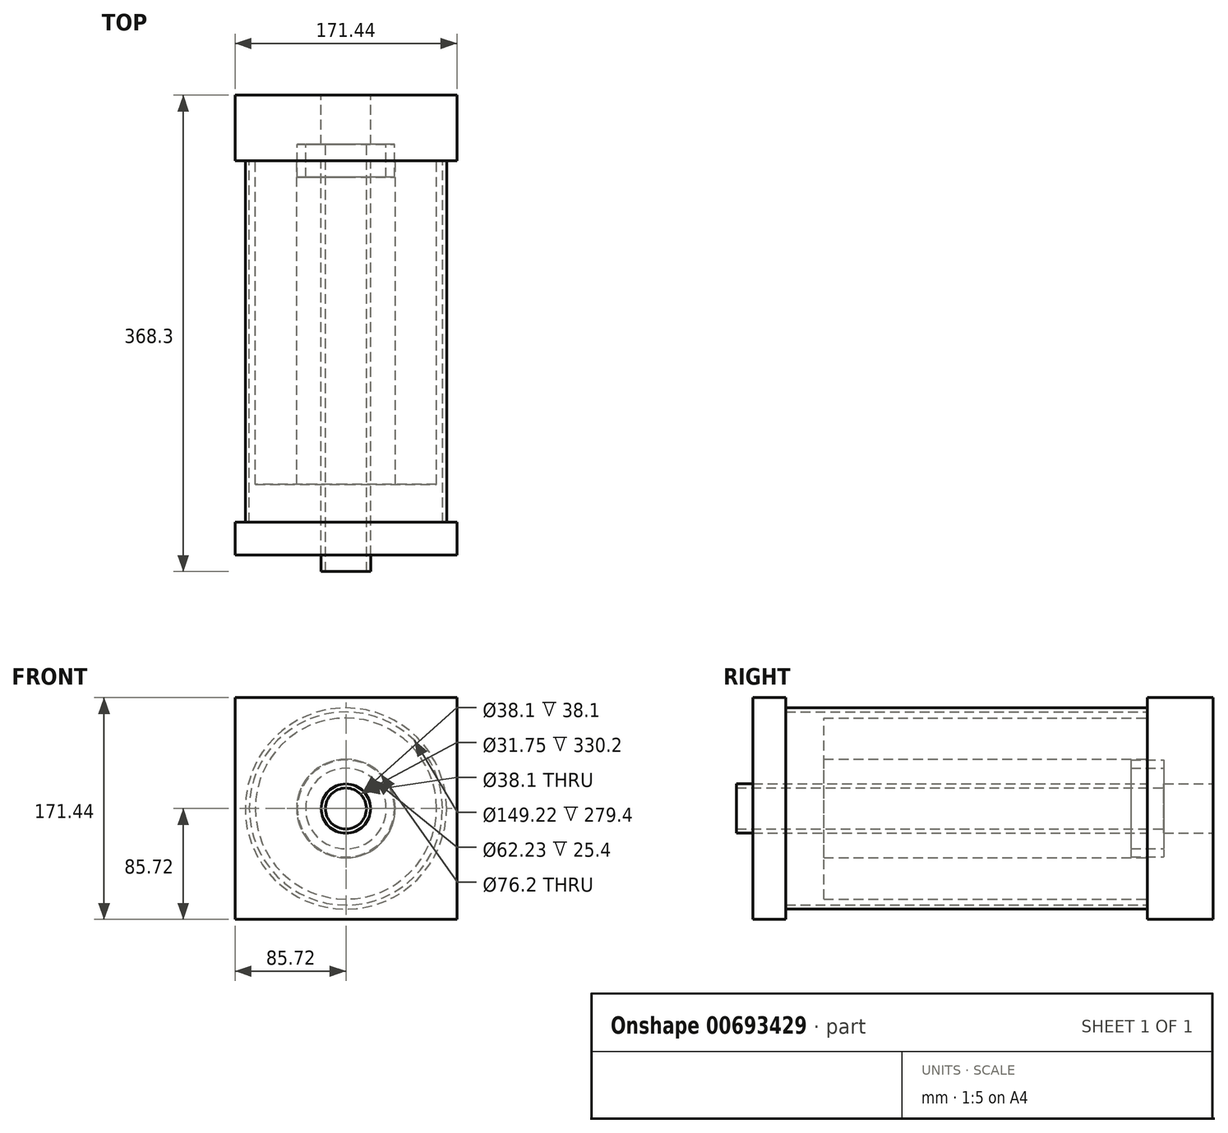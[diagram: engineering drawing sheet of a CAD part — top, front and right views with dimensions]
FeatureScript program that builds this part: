
annotation { "Feature Type Name" : "Feature", "Feature Type Description" : "" }
export const myFeature = defineFeature(function(context is Context, id is Id, definition is map)
    precondition{}
    {
        {
            var Q0;
            Q0=qCreatedBy(makeId("Front.planeOp"),FACE);
            var sketch = newSketch(context, id + "F0", { "sketchPlane" : qUnion([Q0])});
            skCircle(sketch, "E0", {"center": v(0, 0) * mm, "radius": 70 * mm});
            skSolve(sketch);
        }
        {
            var Q0;
            Q0 = qSketchRegion(id + "F0", true);
            extrude(context, id + "F1", {"entities" : qUnion([Q0]), "depth" : 250 * mm, "offsetDistance" : 25.4 * mm});
        }
        {
            var Q0;
            Q0=makeQuery(id+"F1.opExtrude","CAP_FACE",FACE,{"disambiguationData":[OSD([sQuery(id+"F0.wireOp",EDGE,"E0")])],"isStart":true});
            var sketch = newSketch(context, id + "F2", { "sketchPlane" : qUnion([Q0])});
            skCircle(sketch, "E1", {"center": v(0, 0) * mm, "radius": 38.1 * mm});
            skSolve(sketch);
        }
        {
            var Q0;
            Q0 = qSketchRegion(id + "F2", true);
            extrude(context, id + "F3", {"entities" : qUnion([Q0]), "operationType" : NewBodyOperationType.REMOVE, "endBound" : BoundingType.THROUGH_ALL, "oppositeDirection" : true, "depth" : 25.4 * mm, "offsetDistance" : 25.4 * mm});
        }
        {
            var Q0;
            Q0=makeQuery(id+"F1.opExtrude","CAP_FACE",FACE,{"disambiguationData":[OSD([sQuery(id+"F0.wireOp",EDGE,"E0")])],"isStart":true});
            var sketch = newSketch(context, id + "F4", { "sketchPlane" : qUnion([Q0])});
            skCircle(sketch, "E2", {"center": v(0, 0) * mm, "radius": 37.47 * mm});
            skCircle(sketch, "E3", {"center": v(0, 0) * mm, "radius": 31.12 * mm});
            skSolve(sketch);
        }
        {
            var Q0;
            Q0 = qSketchRegion(id + "F4", true);
            extrude(context, id + "F5", {"entities" : qUnion([Q0]), "endBound" : BoundingType.SYMMETRIC, "oppositeDirection" : true, "depth" : 25.4 * mm, "offsetDistance" : 25.4 * mm});
        }
        {
            var Q0;
            Q0=qCreatedBy(makeId("Front.planeOp"),FACE);
            var sketch = newSketch(context, id + "F6", { "sketchPlane" : qUnion([Q0])});
            skCircle(sketch, "E4", {"center": v(0, 0) * mm, "radius": 74.61 * mm});
            skCircle(sketch, "E5", {"center": v(0, 0) * mm, "radius": 77.79 * mm});
            skSolve(sketch);
        }
        {
            var Q0;
            Q0 = qSketchRegion(id + "F6", true);
            extrude(context, id + "F7", {"entities" : qUnion([Q0]), "depth" : 279.4 * mm, "offsetDistance" : 25.4 * mm});
        }
        {
            var Q0;
            Q0=qCreatedBy(makeId("Front.planeOp"),FACE);
            var sketch = newSketch(context, id + "F8", { "sketchPlane" : qUnion([Q0])});
            skLineSegment(sketch, "E6.bottom", {"start": v(-85.73, 85.73) * mm, "end": v(85.73, 85.73) * mm});
            skLineSegment(sketch, "E6.top", {"start": v(-85.73, -85.73) * mm, "end": v(85.73, -85.73) * mm});
            skLineSegment(sketch, "E6.left", {"start": v(-85.73, 85.73) * mm, "end": v(-85.73, -85.73) * mm});
            skLineSegment(sketch, "E6.right", {"start": v(85.73, 85.73) * mm, "end": v(85.73, -85.73) * mm});
            skPoint(sketch, "E6.middle", {"position": v(0, 0) * mm});
            skSolve(sketch);
        }
        {
            var Q0;
            Q0 = qSketchRegion(id + "F8", true);
            extrude(context, id + "F9", {"entities" : qUnion([Q0]), "oppositeDirection" : true, "depth" : 50.8 * mm, "offsetDistance" : 25.4 * mm});
        }
        {
            var Q0;
            Q0=makeQuery(id+"F9.opExtrude","CAP_FACE",FACE,{"disambiguationData":[OSD([sQuery(id+"F8.wireOp",EDGE,"E6.bottom"),sQuery(id+"F8.wireOp",EDGE,"E6.top"),sQuery(id+"F8.wireOp",EDGE,"E6.left"),sQuery(id+"F8.wireOp",EDGE,"E6.right")])],"isStart":false});
            var sketch = newSketch(context, id + "F10", { "sketchPlane" : qUnion([Q0])});
            skCircle(sketch, "E7", {"center": v(0, 0) * mm, "radius": 19.05 * mm});
            skSolve(sketch);
        }
        {
            var Q0;
            Q0 = qSketchRegion(id + "F10", true);
            extrude(context, id + "F11", {"entities" : qUnion([Q0]), "operationType" : NewBodyOperationType.REMOVE, "endBound" : BoundingType.THROUGH_ALL, "oppositeDirection" : true, "depth" : 25.4 * mm, "offsetDistance" : 25.4 * mm});
        }
        {
            var Q0;
            Q0=makeQuery(id+"F9.opExtrude","CAP_FACE",FACE,{"disambiguationData":[OSD([sQuery(id+"F8.wireOp",EDGE,"E6.bottom"),sQuery(id+"F8.wireOp",EDGE,"E6.top"),sQuery(id+"F8.wireOp",EDGE,"E6.left"),sQuery(id+"F8.wireOp",EDGE,"E6.right")])],"isStart":true});
            var sketch = newSketch(context, id + "F12", { "sketchPlane" : qUnion([Q0])});
            skCircle(sketch, "E8", {"center": v(0, 0) * mm, "radius": 19.05 * mm});
            skCircle(sketch, "E9", {"center": v(0, 0) * mm, "radius": 15.88 * mm});
            skSolve(sketch);
        }
        {
            var Q0;
            Q0 = qSketchRegion(id + "F12", true);
            extrude(context, id + "F13", {"entities" : qUnion([Q0]), "operationType" : NewBodyOperationType.ADD, "endBound" : BoundingType.SYMMETRIC, "depth" : 25.4 * mm, "offsetDistance" : 25.4 * mm});
        }
        {
            var Q0;
            Q0=makeQuery(id+"F13.opExtrude","CAP_FACE",FACE,{"disambiguationData":[OSD([sQuery(id+"F12.wireOp",EDGE,"E8"),sQuery(id+"F12.wireOp",EDGE,"E9")])],"isStart":false});
            var sketch = newSketch(context, id + "F14", { "sketchPlane" : qUnion([Q0])});
            skCircle(sketch, "E10", {"center": v(0, 0) * mm, "radius": 19.05 * mm});
            skCircle(sketch, "E11", {"center": v(0, 0) * mm, "radius": 15.88 * mm});
            skSolve(sketch);
        }
        {
            var Q0;
            Q0 = qSketchRegion(id + "F14", true);
            extrude(context, id + "F15", {"entities" : qUnion([Q0]), "operationType" : NewBodyOperationType.ADD, "depth" : 304.8 * mm, "offsetDistance" : 25.4 * mm});
        }
        {
            var Q0;
            Q0=makeQuery(id+"F7.opExtrude","CAP_FACE",FACE,{"disambiguationData":[OSD([sQuery(id+"F6.wireOp",EDGE,"E4"),sQuery(id+"F6.wireOp",EDGE,"E5")])],"isStart":false});
            var sketch = newSketch(context, id + "F16", { "sketchPlane" : qUnion([Q0])});
            skLineSegment(sketch, "E12.bottom", {"start": v(85.72, 85.73) * mm, "end": v(-85.73, 85.73) * mm});
            skLineSegment(sketch, "E12.top", {"start": v(85.73, -85.73) * mm, "end": v(-85.72, -85.73) * mm});
            skLineSegment(sketch, "E12.left", {"start": v(85.72, 85.73) * mm, "end": v(85.73, -85.73) * mm});
            skLineSegment(sketch, "E12.right", {"start": v(-85.73, 85.73) * mm, "end": v(-85.72, -85.73) * mm});
            skPoint(sketch, "E12.middle", {"position": v(0, 0) * mm});
            skCircle(sketch, "E13", {"center": v(0, 0) * mm, "radius": 19.05 * mm});
            skSolve(sketch);
        }
        {
            var Q0;
            Q0 = qSketchRegion(id + "F16", true);
            extrude(context, id + "F17", {"entities" : qUnion([Q0]), "depth" : 25.4 * mm, "offsetDistance" : 25.4 * mm});
        }
    });
